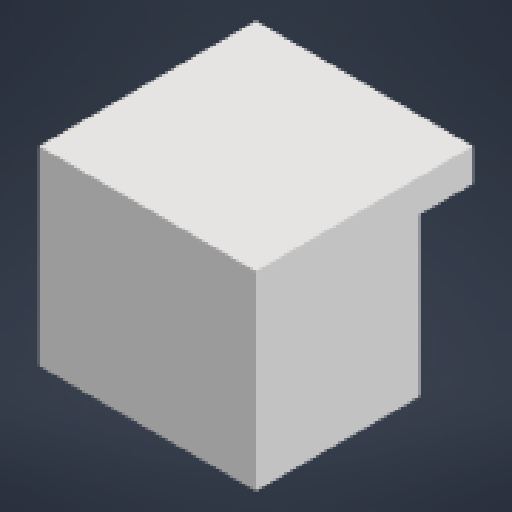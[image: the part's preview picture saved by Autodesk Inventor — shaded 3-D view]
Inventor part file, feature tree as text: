
AUTODESK INVENTOR PART (.ipt)
format: ipt  version: 2024 (Build 280153000, 153)  size: 333,312 bytes
history: native  units: mm
features: sketch x17, extrude x16, other x7, fillet x5, reference x5, projected_geometry x1
ambient origin geometry x8: Origin, YZ Plane, XZ Plane, XY Plane, X Axis, Y Axis, Z Axis, Center Point
bodies: Body1 (feature_tree)
feature tree (51):
  other  "Твердое тело1"
  extrude  "Выдавливание1"  Depth=17.0mm
  extrude  "Выдавливание2"  Depth=17.0mm
  extrude  "Выдавливание5"  Depth=2.0mm
  extrude  "Выдавливание3"  Depth=10.0mm TaperAngle=0.0deg
  extrude  "Выдавливание6"  Depth=1.5mm
  sketch  "Эскиз7"
  other  "РабПлоскость1"
  extrude  "Выдавливание7"  Depth=4.0mm TaperAngle=0.0deg
  extrude  "Выдавливание8"  Depth=10.0mm
  extrude  "Выдавливание9"  Depth=8.0mm
  extrude  "Выдавливание10"  Depth=19.5mm TaperAngle=0.0deg
  fillet  "Сопряжение2"  Radius=19.25mm
  extrude  "Выдавливание11"  Depth=3.0mm
  extrude  "Выдавливание12"  Depth=3.0mm
  extrude  "Выдавливание13"  Depth=4.0mm
  extrude  "Выдавливание14"  Depth=20.0mm
  extrude  "Выдавливание15"  Depth=38.0mm TaperAngle=0.0deg
  sketch  "Эскиз16"
  extrude  "Выдавливание16"  Depth=3.0mm
  fillet  "Сопряжение3"  Radius=27.25mm
  fillet  "Сопряжение4"  Radius=20.5mm
  fillet  "Сопряжение5"  Radius=3.0mm
  fillet  "Сопряжение6"  Radius=12.0mm
  extrude  "Выдавливание17"  Depth=6.5mm TaperAngle=0.0deg
  sketch  "Эскиз1"
  sketch  "Эскиз2"
  sketch  "Эскиз3"
  sketch  "Эскиз5"
  sketch  "Эскиз6"
  projected_geometry  "Спроецированная петля1"
  sketch  "Эскиз8"
  sketch  "Эскиз9"
  reference  "Ссылка3"
  reference  "Ссылка4"
  sketch  "Эскиз10"
  reference  "Ссылка5"
  reference  "Ссылка6"
  sketch  "Эскиз11"
  sketch  "Эскиз12"
  sketch  "Эскиз13"
  sketch  "Эскиз14"
  sketch  "Эскиз15"
  reference  "Ссылка7"
  sketch  "Эскиз17"
  sketch  "Эскиз18"
  parser-record x1  (decoder bookkeeping rows leaked as tree rows — omitted from the tree; the rows remain in map.json)
  other  "manipulator_asembly.iam"
  other  "MG996R SBORKA:1"
  other  "Servo MG996R:1"
  other  "Servo MG996R arm01:1"
note: 1 file-system path scrubbed to <path> (originals preserved in map.json)
